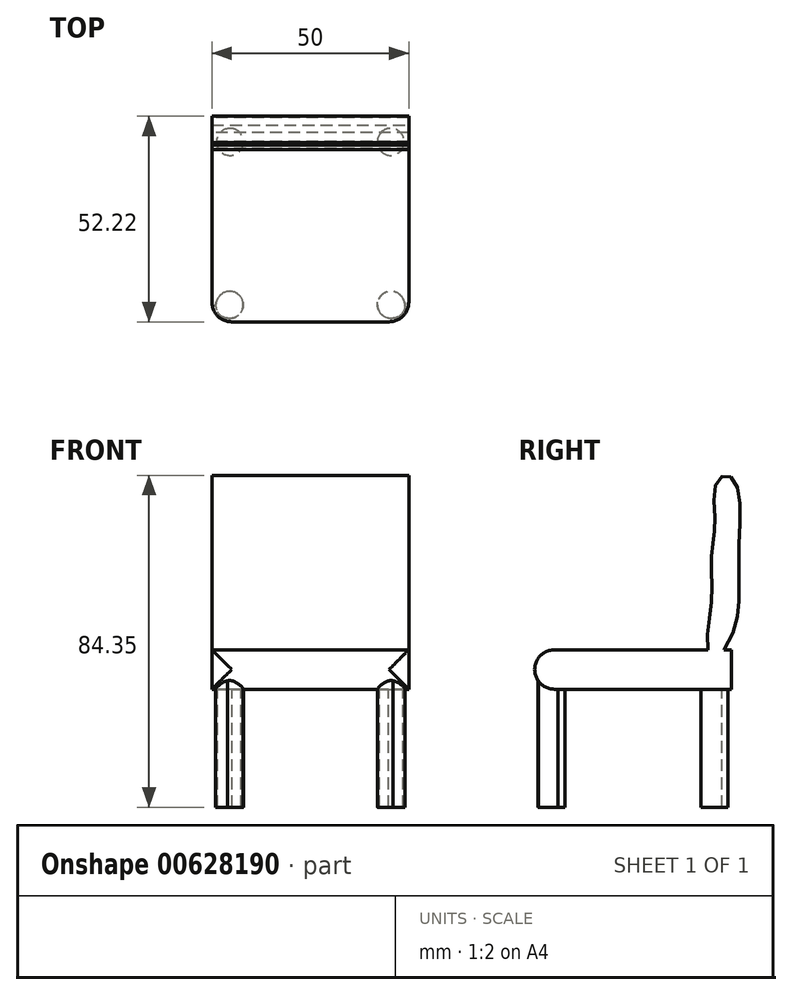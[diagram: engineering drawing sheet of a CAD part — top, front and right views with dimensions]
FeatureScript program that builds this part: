
annotation { "Feature Type Name" : "Feature", "Feature Type Description" : "" }
export const myFeature = defineFeature(function(context is Context, id is Id, definition is map)
    precondition{}
    {
        {
            var Q0;
            Q0=qCreatedBy(makeId("Top.planeOp"),FACE);
            var sketch = newSketch(context, id + "F0", { "sketchPlane" : qUnion([Q0])});
            skLineSegment(sketch, "E0.bottom", {"start": v(-25, -25) * mm, "end": v(25, -25) * mm});
            skLineSegment(sketch, "E0.top", {"start": v(-25, 25) * mm, "end": v(25, 25) * mm});
            skLineSegment(sketch, "E0.left", {"start": v(-25, -25) * mm, "end": v(-25, 25) * mm});
            skLineSegment(sketch, "E0.right", {"start": v(25, -25) * mm, "end": v(25, 25) * mm});
            skPoint(sketch, "E0.middle", {"position": v(0, 0) * mm});
            skSolve(sketch);
        }
        {
            var Q0;
            Q0=makeQuery(id+"F0.imprint","IMPRINT",FACE,{"disambiguationData":[TD([[makeQuery(id+"F0.imprint","IMPRINT",EDGE,{"derivedFrom":sQuery(id+"F0.wireOp",EDGE,"E0.bottom")}),1.0]])]});
            var sketch = newSketch(context, id + "F1", { "sketchPlane" : qUnion([Q0])});
            skCircle(sketch, "E1", {"center": v(20.79, -20.85) * mm, "radius": 3.25 * mm});
            skPoint(sketch, "E1.first.point", {"position": v(23.16, -23.07) * mm});
            skPoint(sketch, "E1.second.point", {"position": v(18.73, -18.33) * mm});
            skPoint(sketch, "E1.third.point", {"position": v(23.01, -18.47) * mm});
            skSolve(sketch);
        }
        {
            var Q0;
            Q0=makeQuery(id+"F0.imprint","IMPRINT",FACE,{"disambiguationData":[TD([[makeQuery(id+"F0.imprint","IMPRINT",EDGE,{"derivedFrom":sQuery(id+"F0.wireOp",EDGE,"E0.bottom")}),1.0]])]});
            var sketch = newSketch(context, id + "F2", { "sketchPlane" : qUnion([Q0])});
            skCircle(sketch, "E2", {"center": v(20.16, 21.1) * mm, "radius": 2.98 * mm});
            skPoint(sketch, "E2.first.point", {"position": v(21.38, 23.82) * mm});
            skPoint(sketch, "E2.second.point", {"position": v(23.05, 20.36) * mm});
            skPoint(sketch, "E2.third.point", {"position": v(20.74, 18.18) * mm});
            skSolve(sketch);
        }
        {
            var Q0;
            Q0=makeQuery(id+"F0.imprint","IMPRINT",FACE,{"disambiguationData":[TD([[makeQuery(id+"F0.imprint","IMPRINT",EDGE,{"derivedFrom":sQuery(id+"F0.wireOp",EDGE,"E0.bottom")}),1.0]])]});
            var sketch = newSketch(context, id + "F3", { "sketchPlane" : qUnion([Q0])});
            skCircle(sketch, "E3", {"center": v(-20.43, 20.69) * mm, "radius": 3.43 * mm});
            skPoint(sketch, "E3.first.point", {"position": v(-21.14, 24.04) * mm});
            skPoint(sketch, "E3.second.point", {"position": v(-23.86, 20.6) * mm});
            skPoint(sketch, "E3.third.point", {"position": v(-18.24, 18.05) * mm});
            skSolve(sketch);
        }
        {
            var Q0;
            Q0=makeQuery(id+"F0.imprint","IMPRINT",FACE,{"disambiguationData":[TD([[makeQuery(id+"F0.imprint","IMPRINT",EDGE,{"derivedFrom":sQuery(id+"F0.wireOp",EDGE,"E0.bottom")}),1.0]])]});
            var sketch = newSketch(context, id + "F4", { "sketchPlane" : qUnion([Q0])});
            skCircle(sketch, "E4", {"center": v(-20.48, -20.7) * mm, "radius": 3.44 * mm});
            skPoint(sketch, "E4.first.point", {"position": v(-23.86, -20.05) * mm});
            skPoint(sketch, "E4.second.point", {"position": v(-19.69, -24.04) * mm});
            skPoint(sketch, "E4.third.point", {"position": v(-17.33, -19.32) * mm});
            skSolve(sketch);
        }
        {
            var Q0;
            Q0=makeQuery(id+"F0.imprint","IMPRINT",FACE,{"disambiguationData":[TD([[makeQuery(id+"F0.imprint","IMPRINT",EDGE,{"derivedFrom":sQuery(id+"F0.wireOp",EDGE,"E0.bottom")}),1.0]])]});
            extrude(context, id + "F5", {"entities" : qUnion([Q0]), "depth" : 10 * mm, "offsetDistance" : 25 * mm});
        }
        {
            var Q0;
            Q0 = qSketchRegion(id + "F1", true);
            extrude(context, id + "F6", {"entities" : qUnion([Q0]), "operationType" : NewBodyOperationType.ADD, "oppositeDirection" : true, "depth" : 30 * mm, "offsetDistance" : 25 * mm});
        }
        {
            var Q0;
            Q0 = qSketchRegion(id + "F3", true);
            var Q1;
            Q1 = qSketchRegion(id + "F2", true);
            var Q2;
            Q2 = qSketchRegion(id + "F4", true);
            extrude(context, id + "F7", {"entities" : qUnion([Q0, Q1, Q2]), "operationType" : NewBodyOperationType.ADD, "oppositeDirection" : true, "depth" : 30 * mm, "offsetDistance" : 25 * mm});
        }
        {
            var Q0;
            Q0=qCreatedBy(makeId("Right.planeOp"),FACE);
            var sketch = newSketch(context, id + "F8", { "sketchPlane" : qUnion([Q0])});
            skFitSpline(sketch, "E5", {"points": [v(20.6, 7.71) * mm, v(25.5, 14.79) * mm, v(26.95, 24.22) * mm, v(26.95, 37.83) * mm, v(26.58, 51.08) * mm, v(23.68, 54.34) * mm, v(20.96, 51.99) * mm, v(20.78, 42.91) * mm, v(20.23, 36.93) * mm, v(19.87, 29.85) * mm, v(19.87, 21.14) * mm, v(18.78, 11.52) * mm, v(20.6, 7.71) * mm]});
            skSolve(sketch);
        }
        {
            var Q0;
            Q0 = qSketchRegion(id + "F8", true);
            extrude(context, id + "F9", {"entities" : qUnion([Q0]), "operationType" : NewBodyOperationType.ADD, "depth" : 25 * mm, "offsetDistance" : 25 * mm});
        }
        {
            var Q0;
            Q0=makeQuery(id+"F5.opExtrude","SWEPT_BODY",BODY,{"disambiguationData":[OSD([sQuery(id+"F0.wireOp",EDGE,"E0.bottom"),sQuery(id+"F0.wireOp",EDGE,"E0.top"),sQuery(id+"F0.wireOp",EDGE,"E0.left"),sQuery(id+"F0.wireOp",EDGE,"E0.right")])]});
            var Q1;
            Q1=qCreatedBy(makeId("Right.planeOp"),FACE);
            mirror(context, id + "F10", {"operationType" : NewBodyOperationType.ADD, "entities" : qUnion([Q0]), "mirrorPlane" : qUnion([Q1])});
        }
        {
            var Q0;
            Q0=makeQuery(id+"F5.opExtrude","SWEPT_FACE",FACE,{"disambiguationData":[OSD([sQuery(id+"F0.wireOp",EDGE,"E0.bottom")])]});
            fillet(context, id + "F11", {"entities" : qUnion([Q0]), "radius" : 5 * mm, "tangentPropagation" : true, "allowEdgeOverflow" : false});
        }
    });
